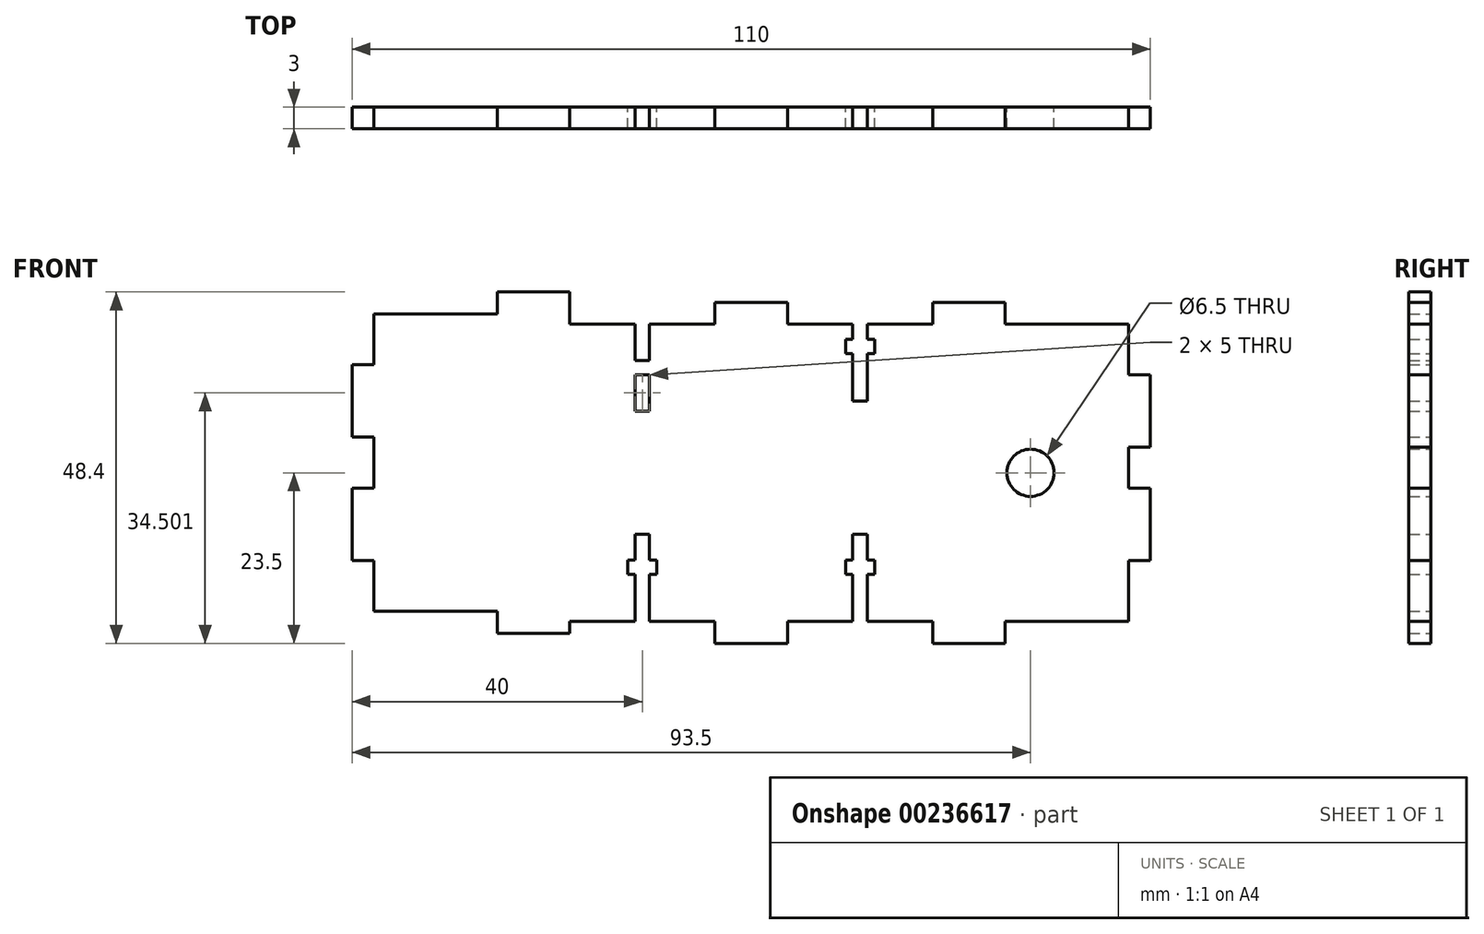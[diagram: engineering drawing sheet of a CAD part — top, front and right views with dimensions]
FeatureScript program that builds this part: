
annotation { "Feature Type Name" : "Feature", "Feature Type Description" : "" }
export const myFeature = defineFeature(function(context is Context, id is Id, definition is map)
    precondition{}
    {
        {
            var Q0;
            Q0=qCreatedBy(makeId("Front.planeOp"),FACE);
            var sketch = newSketch(context, id + "F0", { "sketchPlane" : qUnion([Q0])});
            skLineSegment(sketch, "E0.MirrorCS", {"start": v(-8, -0.02) * mm, "end": v(-8, -3.02) * mm});
            skLineSegment(sketch, "E1.MirrorCS", {"start": v(-38, 1.38) * mm, "end": v(-38, -1.62) * mm});
            skLineSegment(sketch, "E2.MirrorCS", {"start": v(-28, -1.62) * mm, "end": v(-28, -0.02) * mm});
            skLineSegment(sketch, "E3.MirrorCS", {"start": v(-28, -0.02) * mm, "end": v(-19, -0.02) * mm});
            skLineSegment(sketch, "E4.MirrorCS", {"start": v(-55, 1.38) * mm, "end": v(-38, 1.38) * mm});
            skLineSegment(sketch, "E5.MirrorCS", {"start": v(-38, -1.62) * mm, "end": v(-28, -1.62) * mm});
            skLineSegment(sketch, "E6", {"start": v(-55, 1.38) * mm, "end": v(-55, 8.38) * mm});
            skLineSegment(sketch, "E7", {"start": v(-55, 8.38) * mm, "end": v(-58, 8.38) * mm});
            skLineSegment(sketch, "E8", {"start": v(-58, 8.38) * mm, "end": v(-58, 18.38) * mm});
            skLineSegment(sketch, "E9", {"start": v(-58, 18.38) * mm, "end": v(-55, 18.38) * mm});
            skLineSegment(sketch, "E10", {"start": v(-55, 18.38) * mm, "end": v(-55, 25.38) * mm});
            skLineSegment(sketch, "E11", {"start": v(-55, 25.38) * mm, "end": v(-58, 25.38) * mm});
            skLineSegment(sketch, "E12", {"start": v(-58, 25.38) * mm, "end": v(-58, 35.38) * mm});
            skLineSegment(sketch, "E13", {"start": v(-58, 35.38) * mm, "end": v(-55, 35.38) * mm});
            skLineSegment(sketch, "E14", {"start": v(-55, 35.38) * mm, "end": v(-55, 42.38) * mm});
            skLineSegment(sketch, "E15.MirrorCS", {"start": v(-8, 40.98) * mm, "end": v(-8, 43.98) * mm});
            skLineSegment(sketch, "E16.MirrorCS", {"start": v(-38, 42.38) * mm, "end": v(-38, 45.38) * mm});
            skLineSegment(sketch, "E17.MirrorCS", {"start": v(-28, 45.38) * mm, "end": v(-28, 40.98) * mm});
            skLineSegment(sketch, "E18.MirrorCS", {"start": v(-38, 45.38) * mm, "end": v(-28, 45.38) * mm});
            skLineSegment(sketch, "E19.MirrorCS", {"start": v(-55, 42.38) * mm, "end": v(-38, 42.38) * mm});
            skLineSegment(sketch, "E20.bottom", {"start": v(-19, 11.98) * mm, "end": v(-17, 11.98) * mm});
            skLineSegment(sketch, "E20.left", {"start": v(-19, 11.98) * mm, "end": v(-19, 8.48) * mm});
            skLineSegment(sketch, "E20.right", {"start": v(-17, 11.98) * mm, "end": v(-17, 8.48) * mm});
            skLineSegment(sketch, "E21.bottom", {"start": v(-20, 8.48) * mm, "end": v(-19, 8.48) * mm});
            skLineSegment(sketch, "E21.top", {"start": v(-20, 6.48) * mm, "end": v(-19, 6.48) * mm});
            skLineSegment(sketch, "E21.left", {"start": v(-20, 8.48) * mm, "end": v(-20, 6.48) * mm});
            skLineSegment(sketch, "E21.right", {"start": v(-16, 8.48) * mm, "end": v(-16, 6.48) * mm});
            skLineSegment(sketch, "E22.trimOffspring", {"start": v(-17, -0.02) * mm, "end": v(-8, -0.02) * mm});
            skLineSegment(sketch, "E23.trimOffspring", {"start": v(-17, 6.48) * mm, "end": v(-16, 6.48) * mm});
            skLineSegment(sketch, "E24.trimOffspring", {"start": v(-17, 6.48) * mm, "end": v(-17, -0.02) * mm});
            skLineSegment(sketch, "E25.trimOffspring", {"start": v(-19, 6.48) * mm, "end": v(-19, -0.02) * mm});
            skLineSegment(sketch, "E26.trimOffspring", {"start": v(-17, 8.48) * mm, "end": v(-16, 8.48) * mm});
            skPoint(sketch, "E27.orphan", {"position": v(0, 69.16) * mm});
            skPoint(sketch, "E28.endSnap0", {"position": v(-56.5, 8.38) * mm});
            skLineSegment(sketch, "E29", {"start": v(-8, 43.98) * mm, "end": v(2, 43.98) * mm});
            skLineSegment(sketch, "E30", {"start": v(2, 43.98) * mm, "end": v(2, 40.98) * mm});
            skLineSegment(sketch, "E31", {"start": v(2, 40.98) * mm, "end": v(11, 40.98) * mm});
            skLineSegment(sketch, "E32", {"start": v(-8, -3.02) * mm, "end": v(2, -3.02) * mm});
            skLineSegment(sketch, "E33", {"start": v(2, -3.02) * mm, "end": v(2, -0.02) * mm});
            skLineSegment(sketch, "E34", {"start": v(2, -0.02) * mm, "end": v(11, -0.02) * mm});
            skLineSegment(sketch, "E35", {"start": v(22, 40.98) * mm, "end": v(22, 43.98) * mm});
            skLineSegment(sketch, "E36", {"start": v(22, 43.98) * mm, "end": v(32, 43.98) * mm});
            skLineSegment(sketch, "E37", {"start": v(32, 43.98) * mm, "end": v(32, 40.98) * mm});
            skLineSegment(sketch, "E38", {"start": v(32, 40.98) * mm, "end": v(49, 40.98) * mm});
            skLineSegment(sketch, "E39", {"start": v(22, -0.02) * mm, "end": v(22, -3.02) * mm});
            skLineSegment(sketch, "E40", {"start": v(22, -3.02) * mm, "end": v(32, -3.02) * mm});
            skLineSegment(sketch, "E41", {"start": v(32, -3.02) * mm, "end": v(32, -0.02) * mm});
            skLineSegment(sketch, "E42", {"start": v(32, -0.02) * mm, "end": v(49, -0.02) * mm});
            skLineSegment(sketch, "E43", {"start": v(49, 40.98) * mm, "end": v(49, 33.98) * mm});
            skLineSegment(sketch, "E44", {"start": v(49, 33.98) * mm, "end": v(52, 33.98) * mm});
            skLineSegment(sketch, "E45", {"start": v(52, 33.98) * mm, "end": v(52, 23.98) * mm});
            skLineSegment(sketch, "E46", {"start": v(52, 23.98) * mm, "end": v(49, 23.98) * mm});
            skLineSegment(sketch, "E47", {"start": v(49, 23.98) * mm, "end": v(49, 18.38) * mm});
            skLineSegment(sketch, "E48", {"start": v(49, 18.38) * mm, "end": v(52, 18.38) * mm});
            skLineSegment(sketch, "E49", {"start": v(52, 18.38) * mm, "end": v(52, 8.38) * mm});
            skLineSegment(sketch, "E50", {"start": v(52, 8.38) * mm, "end": v(49, 8.38) * mm});
            skLineSegment(sketch, "E51", {"start": v(49, 8.38) * mm, "end": v(49, -0.02) * mm});
            skLineSegment(sketch, "E52", {"start": v(-3, 61.79) * mm, "end": v(-3, -7.76) * mm, "construction": true});
            skLineSegment(sketch, "E53.MirrorCS", {"start": v(14, 6.48) * mm, "end": v(13, 6.48) * mm});
            skLineSegment(sketch, "E54.MirrorCS", {"start": v(14, 38.88) * mm, "end": v(13, 38.88) * mm});
            skLineSegment(sketch, "E55.MirrorCS", {"start": v(11, 6.48) * mm, "end": v(10, 6.48) * mm});
            skLineSegment(sketch, "E56.MirrorCS", {"start": v(10, 8.48) * mm, "end": v(10, 6.48) * mm});
            skLineSegment(sketch, "E57.MirrorCS", {"start": v(11, 8.48) * mm, "end": v(10, 8.48) * mm});
            skLineSegment(sketch, "E58.MirrorCS", {"start": v(14, 8.48) * mm, "end": v(14, 6.48) * mm});
            skLineSegment(sketch, "E59.MirrorCS", {"start": v(14, 36.88) * mm, "end": v(14, 38.88) * mm});
            skLineSegment(sketch, "E60.MirrorCS", {"start": v(14, 8.48) * mm, "end": v(13, 8.48) * mm});
            skLineSegment(sketch, "E61.MirrorCS", {"start": v(14, 36.88) * mm, "end": v(13, 36.88) * mm});
            skLineSegment(sketch, "E62.MirrorCS", {"start": v(13, 11.98) * mm, "end": v(11, 11.98) * mm});
            skLineSegment(sketch, "E63.MirrorCS", {"start": v(13, 30.38) * mm, "end": v(11, 30.38) * mm});
            skLineSegment(sketch, "E64.MirrorCS", {"start": v(13, 11.98) * mm, "end": v(13, 8.48) * mm});
            skLineSegment(sketch, "E65.MirrorCS", {"start": v(11, 11.98) * mm, "end": v(11, 8.48) * mm});
            skLineSegment(sketch, "E66.MirrorCS", {"start": v(13, 6.48) * mm, "end": v(13, -0.02) * mm});
            skLineSegment(sketch, "E67.MirrorCS", {"start": v(11, 6.48) * mm, "end": v(11, -0.02) * mm});
            skLineSegment(sketch, "E68.MirrorCS", {"start": v(11, 35.88) * mm, "end": v(11, 36.88) * mm});
            skLineSegment(sketch, "E69.MirrorCS", {"start": v(13, 30.38) * mm, "end": v(13, 36.88) * mm});
            skLineSegment(sketch, "E70.MirrorCS", {"start": v(11, 30.38) * mm, "end": v(11, 36.88) * mm});
            skLineSegment(sketch, "E71.MirrorCS", {"start": v(13, 38.88) * mm, "end": v(13, 40.98) * mm});
            skLineSegment(sketch, "E72.trimOffspring", {"start": v(13, 40.98) * mm, "end": v(22, 40.98) * mm});
            skLineSegment(sketch, "E73.trimOffspring", {"start": v(13, -0.02) * mm, "end": v(22, -0.02) * mm});
            skLineSegment(sketch, "E74", {"start": v(12, 30.38) * mm, "end": v(12, 38.73) * mm, "construction": true});
            skLineSegment(sketch, "E75.MirrorCS", {"start": v(10, 38.88) * mm, "end": v(11, 38.88) * mm});
            skLineSegment(sketch, "E76.MirrorCS", {"start": v(10, 36.88) * mm, "end": v(10, 38.88) * mm});
            skLineSegment(sketch, "E77.MirrorCS", {"start": v(10, 36.88) * mm, "end": v(11, 36.88) * mm});
            skLineSegment(sketch, "E78.trimOffspring", {"start": v(11, 38.88) * mm, "end": v(11, 40.98) * mm});
            skLineSegment(sketch, "E79", {"start": v(49, 40.98) * mm, "end": v(22, -0.02) * mm, "construction": true});
            skLineSegment(sketch, "E80", {"start": v(22, 40.98) * mm, "end": v(49, -0.02) * mm, "construction": true});
            skLineSegment(sketch, "E81", {"start": v(-28, 40.98) * mm, "end": v(-19, 40.98) * mm});
            skLineSegment(sketch, "E82", {"start": v(-18, 40.98) * mm, "end": v(-18, 20.75) * mm, "construction": true});
            skLineSegment(sketch, "E83.top", {"start": v(-19, 28.98) * mm, "end": v(-17, 28.98) * mm});
            skLineSegment(sketch, "E83.left", {"start": v(-19, 40.98) * mm, "end": v(-19, 28.98) * mm});
            skLineSegment(sketch, "E83.right", {"start": v(-17, 40.98) * mm, "end": v(-17, 28.98) * mm});
            skPoint(sketch, "E84.orphan", {"position": v(-17, 44.32) * mm});
            skLineSegment(sketch, "E85.trimOffspring", {"start": v(-17, 40.98) * mm, "end": v(-8, 40.98) * mm});
            skLineSegment(sketch, "E86.bottom", {"start": v(-20, 35.98) * mm, "end": v(-16, 35.98) * mm});
            skLineSegment(sketch, "E86.top", {"start": v(-20, 33.98) * mm, "end": v(-16, 33.98) * mm});
            skLineSegment(sketch, "E86.left", {"start": v(-20, 35.98) * mm, "end": v(-20, 33.98) * mm});
            skLineSegment(sketch, "E86.right", {"start": v(-16, 35.98) * mm, "end": v(-16, 33.98) * mm});
            skLineSegment(sketch, "E87", {"start": v(-20, 34.98) * mm, "end": v(-16, 34.98) * mm, "construction": true});
            skCircle(sketch, "E88", {"center": v(35.5, 20.48) * mm, "radius": 3.25 * mm});
            skSolve(sketch);
        }
        {
            var Q0;
            Q0=qSketchRegion(id+"F0",true);
            extrude(context, id + "F1", {"entities" : qUnion([Q0]), "endBound" : BoundingType.SYMMETRIC, "depth" : 3 * mm});
        }
    });
